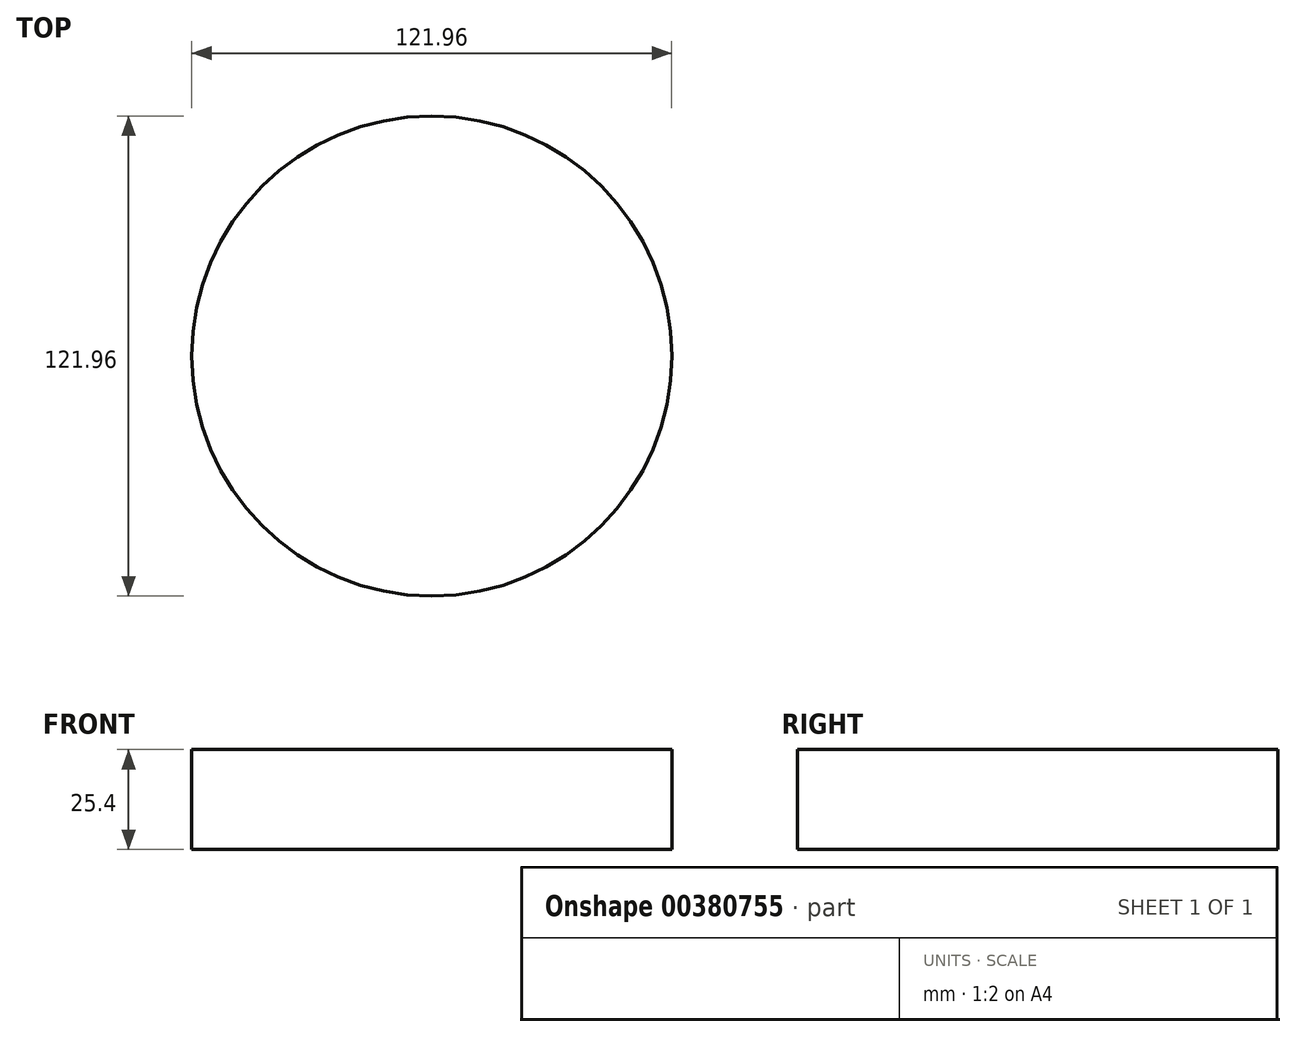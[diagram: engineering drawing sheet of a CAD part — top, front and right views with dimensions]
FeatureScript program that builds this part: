
annotation { "Feature Type Name" : "Feature", "Feature Type Description" : "" }
export const myFeature = defineFeature(function(context is Context, id is Id, definition is map)
    precondition{}
    {
        {
            var Q0;
            Q0=qCreatedBy(makeId("Top.planeOp"),FACE);
            var sketch = newSketch(context, id + "F0", { "sketchPlane" : qUnion([Q0])});
            skCircle(sketch, "E0", {"center": v(0, 0) * mm, "radius": 60.98 * mm});
            skSolve(sketch);
        }
        {
            var Q0;
            Q0 = qSketchRegion(id + "F0", true);
            extrude(context, id + "F1", {"entities" : qUnion([Q0]), "depth" : 25.4 * mm});
        }
    });
